# Revit family: Electronics_Commercial-Loudspeakers_Biamp_Compact-Compression-Driver-Horn_H20
name_source: partatom
category: Communication Devices
units: mm (PartAtom-declared; Revit-internal decimal feet)

## family parameters
Cut with Voids When Loaded = No
Host = Face
Maintain Annotation Orientation = No
OmniClass Number = 23.85.10.11.14.14.14
Part Type = Normal
Room Calculation Point = No
Round Connector Dimension = Use Diameter
Shared = No

## types (1)
- H20-G
    Bracket Material = Biamp - Metal - Gray
    Compliance = IEC 62368-1 certifed
    Connector Description = Conductor; 13V 20W 8 Ω Rated Impedance, 70/100V operation
    Controls = Wattage / low impedance selector switch
    Default Elevation = 1219 mm
    Depth = 230 mm
    Description = H20-G Compact Compression Driver Horn
    Environmental Rating = IP66 per IEC 60529
    Finish = Refer to the Technical Drawings (page 3)
    Height = 200 mm
    Housing Material = Biamp - Plastic - Gray
    Input Connection = 2 x 0.3 mm2 conductor 1 m (39.3) cable
    Manufacturer = Biamp
    Model = H20-G
    Mounting Provisions = U-Bracket
    Nominal Beamwidth  (H x V) = 85° x 85°
    Nominal Continuous Power Handling = 13 V  (20 W, 8 Ω rated Impedance)
    Nominal Maximum SPL (Processed) = 1m - Peak - 124dB; Continuous - 118dB
    Operating Environment = Indoor or Outdoor Direct Exposure
    Operating Mode = Passive with selectable low-impedance or 70 V/100 V operation, Single-amplifed with DSP
    Operating Range (-10 dB) = 490 Hz to 6.7 kHz
    Product Documentation Link = https://downloads.biamp.com
    Product Page URL = https://www.biamp.com
    Product data url = https://bimobject.com
    Protection = Internal DC-blocking capacitor
    Rated Continuous Voltage = 12.6 V (22 dBV)
    Rated Maximum SPL (Processed) = 1m - Peak - 130dB; Continuous - 118dB
    Recommended Amplifers = 20 W - 40 W, 8 Ω (13 V - 18 V)
    Required Accessories = 425 Hz, 6 dB / oct. Butterworth high pass flter; DSP preset
    Sensitivity = 107 dB (2.83 V);107 dB (1 W, 8 Ω)
    Transducer = MF: 1 x 1.4 (36 mm) voice coil compression driver
    Transformer = 70 V: 20 W, 10 W, 5 W, 2.5 W, 1.25 W; 100 V: 20 W, 10 W, 5 W, 2.5 W
    URL = https://www.biamp.com
    Weight = 3.09 lb
    Width = 200 mm

## geometry (parser evidence)
native form markers: Sweep x6
no freeform markers — native parametric forms only
